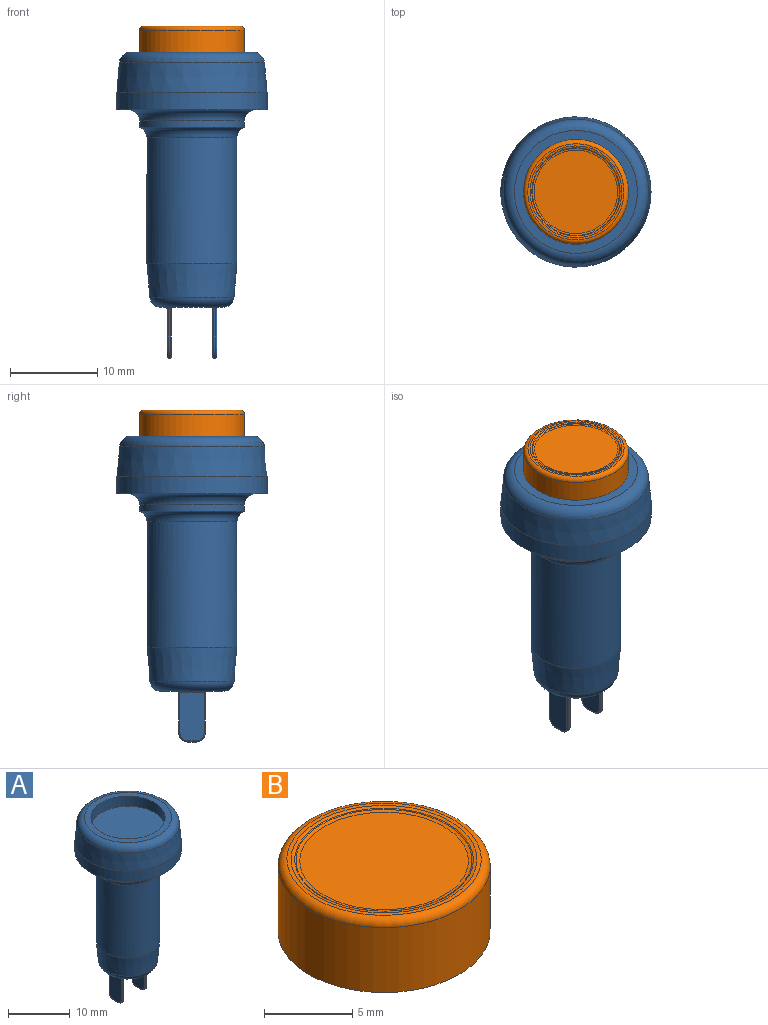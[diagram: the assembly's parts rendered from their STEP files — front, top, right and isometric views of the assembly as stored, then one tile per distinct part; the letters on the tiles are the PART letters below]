
ASSEMBLY  parts=2 mates=1
PART A: 64 faces, bbox 18x18x35.1 mm
  f0: plane 7.1x7.1mm, normal (0,0,-1), area 34.8mm2, adj f20,f34,f35,f38,f39,f42,f43,f44
  f1: plane 14.07x14.07mm, normal (0,0,1), area 42.4mm2, adj f5,f23
  f2: cone r=8.6mm half-angle=5deg, axis (0,0,-1), area 181.9mm2, adj f3,f23
  f3: cylinder r=8.6mm len=17.2mm, axis (0,0,-1), area 109.8mm2, adj f2,f4
  f4: plane 17.2x17.2mm, normal (0,0,-1), area 66.3mm2, adj f3,f22
  f5: cylinder r=6mm len=12mm, axis (0,0,1), area 75.4mm2, adj f1,f6
  f6: plane 12x12mm, normal (0,0,1), area 113.1mm2, adj f5
  f7: cylinder r=6mm len=12mm, axis (0,0,1), area 27.5mm2, adj f21,f22
  f8: cylinder r=5.15mm len=14.4mm, axis (0,0,1), area 466mm2, adj f9,f21
  f9: cone r=5.15mm half-angle=5deg, axis (0,0,1), area 120.7mm2, adj f8,f20
  f10: plane 5.55x2.75mm, normal (1,0,0), area 14.9mm2, adj f28,f30,f31,f36,f39,f40
  f11: plane 4.68x0.25mm, normal (0,-1,0), area 1.2mm2, adj f26,f40,f41,f45
  f12: plane 5.55x2.75mm, normal (-1,0,0), area 14.9mm2, adj f29,f32,f33,f37,f41,f42
  f13: plane 4.68x0.25mm, normal (0,1,0), area 1.2mm2, adj f27,f30,f33,f34
  f14: plane 1x0.25mm, normal (0,0,-1), area 0.2mm2, adj f26,f27,f31,f32
  f15: plane 4.68x0.25mm, normal (0,-1,0), area 1.2mm2, adj f25,f57,f60,f63
  f16: plane 5.55x2.75mm, normal (-1,0,0), area 14.9mm2, adj f46,f48,f49,f53,f57,f58
  f17: plane 4.68x0.25mm, normal (0,1,0), area 1.2mm2, adj f24,f49,f50,f51
  f18: plane 5.55x2.75mm, normal (1,0,0), area 14.9mm2, adj f47,f51,f52,f56,f59,f60
  f19: plane 1x0.25mm, normal (0,0,-1), area 0.2mm2, adj f24,f25,f48,f52
  f20: torus R=3.55mm, axis (0,0,-1), area 51.3mm2, adj f0,f9
  f21: torus R=6.42mm, axis (0,0,1), area 53.6mm2, adj f7,f8
  f22: torus R=7.27mm, axis (0,0,1), area 81mm2, adj f4,f7
  f23: torus R=7.04mm, axis (0,0,1), area 92.5mm2, adj f1,f2
  f24: cylinder r=1mm len=1mm, axis (-1,0,0), area 0.4mm2, adj f17,f19,f46,f47
  f25: cylinder r=1mm len=1mm, axis (1,0,0), area 0.4mm2, adj f15,f19,f53,f56
  f26: cylinder r=1mm len=1mm, axis (1,0,0), area 0.4mm2, adj f11,f14,f36,f37
  f27: cylinder r=1mm len=1mm, axis (-1,0,0), area 0.4mm2, adj f13,f14,f28,f29
  f28: torus R=0.88mm, axis (1,0,0), area 0.3mm2, adj f10,f27,f30,f31
  f29: torus R=0.88mm, axis (1,0,0), area 0.3mm2, adj f12,f27,f32,f33
  f30: cylinder r=0.12mm len=4.68mm, axis (0,0,-1), area 0.9mm2, adj f10,f13,f28,f35
  f31: cylinder r=0.12mm len=1mm, axis (0,1,0), area 0.2mm2, adj f10,f14,f28,f36
  f32: cylinder r=0.12mm len=1mm, axis (0,-1,0), area 0.2mm2, adj f12,f14,f29,f37
  f33: cylinder r=0.12mm len=4.68mm, axis (0,0,1), area 0.9mm2, adj f12,f13,f29,f38
  f34: cylinder r=0.12mm len=0.25mm, axis (1,0,0), area 0mm2, adj f0,f13,f35,f38
  f35: torus R=0.25mm, axis (0,0,-1), area 0.1mm2, adj f0,f30,f34,f39
  f36: torus R=0.88mm, axis (1,0,0), area 0.3mm2, adj f10,f26,f31,f40
  f37: torus R=0.88mm, axis (1,0,0), area 0.3mm2, adj f12,f26,f32,f41
  f38: torus R=0.25mm, axis (0,0,-1), area 0.1mm2, adj f0,f33,f34,f42
  f39: cylinder r=0.12mm len=2.75mm, axis (0,-1,0), area 0.5mm2, adj f0,f10,f35,f43
  f40: cylinder r=0.12mm len=4.68mm, axis (0,0,-1), area 0.9mm2, adj f10,f11,f36,f43
  f41: cylinder r=0.12mm len=4.68mm, axis (0,0,1), area 0.9mm2, adj f11,f12,f37,f44
  f42: cylinder r=0.12mm len=2.75mm, axis (0,1,0), area 0.5mm2, adj f0,f12,f38,f44
  f43: torus R=0.25mm, axis (0,0,-1), area 0.1mm2, adj f0,f39,f40,f45
  f44: torus R=0.25mm, axis (0,0,-1), area 0.1mm2, adj f0,f41,f42,f45
  f45: cylinder r=0.12mm len=0.25mm, axis (-1,0,0), area 0mm2, adj f0,f11,f43,f44
  f46: torus R=0.88mm, axis (1,0,0), area 0.3mm2, adj f16,f24,f48,f49
  f47: torus R=0.88mm, axis (1,0,0), area 0.3mm2, adj f18,f24,f51,f52
  f48: cylinder r=0.12mm len=1mm, axis (0,-1,0), area 0.2mm2, adj f16,f19,f46,f53
  f49: cylinder r=0.12mm len=4.68mm, axis (0,0,-1), area 0.9mm2, adj f16,f17,f46,f54
  f50: cylinder r=0.12mm len=0.25mm, axis (1,0,0), area 0mm2, adj f0,f17,f54,f55
  f51: cylinder r=0.12mm len=4.68mm, axis (0,0,1), area 0.9mm2, adj f17,f18,f47,f55
  f52: cylinder r=0.12mm len=1mm, axis (0,1,0), area 0.2mm2, adj f18,f19,f47,f56
  f53: torus R=0.88mm, axis (1,0,0), area 0.3mm2, adj f16,f25,f48,f57
  f54: torus R=0.25mm, axis (0,0,-1), area 0.1mm2, adj f0,f49,f50,f58
  f55: torus R=0.25mm, axis (0,0,-1), area 0.1mm2, adj f0,f50,f51,f59
  f56: torus R=0.88mm, axis (1,0,0), area 0.3mm2, adj f18,f25,f52,f60
  f57: cylinder r=0.12mm len=4.68mm, axis (0,0,-1), area 0.9mm2, adj f15,f16,f53,f61
  f58: cylinder r=0.12mm len=2.75mm, axis (0,1,0), area 0.5mm2, adj f0,f16,f54,f61
  f59: cylinder r=0.12mm len=2.75mm, axis (0,-1,0), area 0.5mm2, adj f0,f18,f55,f62
  f60: cylinder r=0.12mm len=4.68mm, axis (0,0,1), area 0.9mm2, adj f15,f18,f56,f62
  f61: torus R=0.25mm, axis (0,0,-1), area 0.1mm2, adj f0,f57,f58,f63
  f62: torus R=0.25mm, axis (0,0,-1), area 0.1mm2, adj f0,f59,f60,f63
  f63: cylinder r=0.12mm len=0.25mm, axis (-1,0,0), area 0mm2, adj f0,f15,f61,f62
PART B: 8 faces, bbox 13x13x5 mm
  f0: cylinder r=6mm len=12mm, axis (0,0,-1), area 169.6mm2, adj f2,f7
  f1: plane 11x11mm, normal (0,0,1), area 8.1mm2, adj f5,f7
  f2: plane 12x12mm, normal (0,0,-1), area 113.1mm2, adj f0
  f3: cone r=5.15mm half-angle=65deg, axis (0,0,1), area 2.3mm2, adj f5,f6
  f4: plane 9.54x9.54mm, normal (0,0,1), area 71.5mm2, adj f6
  f5: torus R=5.26mm, axis (0,0,1), area 7.1mm2, adj f1,f3
  f6: torus R=4.77mm, axis (0,0,1), area 6.7mm2, adj f3,f4
  f7: torus R=5.5mm, axis (0,0,1), area 28.7mm2, adj f0,f1
PLACE A at identity fixed
PLACE B t=(0,0,2.57)mm
MATE fastened B.f0 <-> A.f5  axis (0,0,-1) through (0,0,2.57)mm
